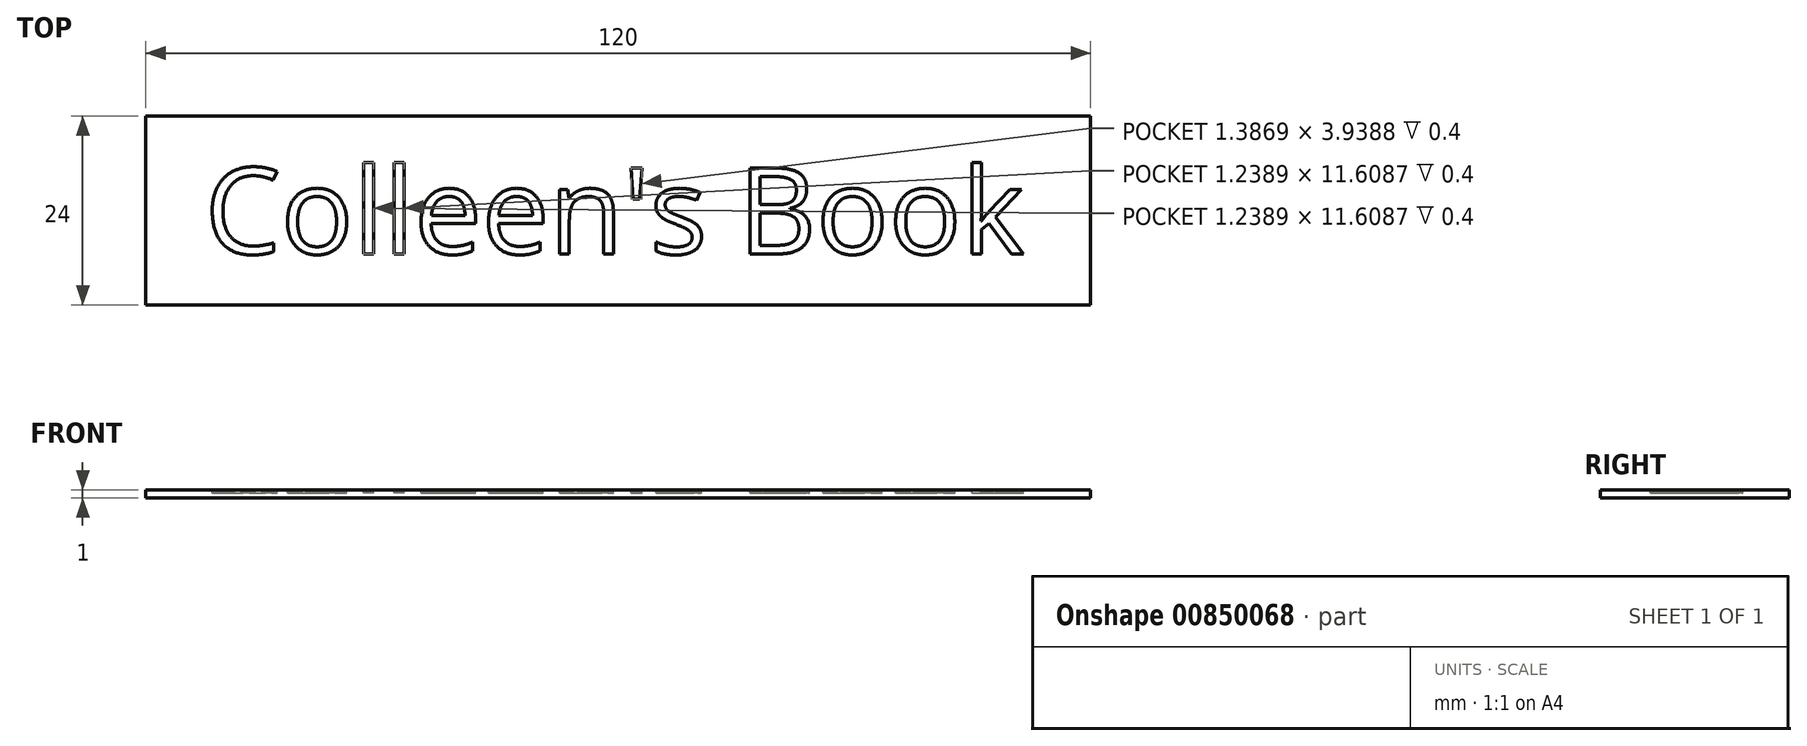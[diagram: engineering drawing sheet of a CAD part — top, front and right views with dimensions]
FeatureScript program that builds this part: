
annotation { "Feature Type Name" : "Feature", "Feature Type Description" : "" }
export const myFeature = defineFeature(function(context is Context, id is Id, definition is map)
    precondition{}
    {
        {
            var Q0;
            Q0=qCreatedBy(makeId("Top.planeOp"),FACE);
            var sketch = newSketch(context, id + "F0", { "sketchPlane" : qUnion([Q0])});
            skLineSegment(sketch, "E0.bottom", {"start": v(60, 12) * mm, "end": v(-60, 12) * mm});
            skLineSegment(sketch, "E0.top", {"start": v(60, -12) * mm, "end": v(-60, -12) * mm});
            skLineSegment(sketch, "E0.left", {"start": v(60, 12) * mm, "end": v(60, -12) * mm});
            skLineSegment(sketch, "E0.right", {"start": v(-60, 12) * mm, "end": v(-60, -12) * mm});
            skPoint(sketch, "E0.middle", {"position": v(0, 0) * mm});
            skSolve(sketch);
        }
        {
            var Q0;
            Q0 = qSketchRegion(id + "F0", true);
            extrude(context, id + "F1", {"entities" : qUnion([Q0]), "depth" : 1 * mm, "offsetDistance" : 25 * mm});
        }
        {
            var Q0;
            Q0=makeQuery(id+"F1.opExtrude","CAP_FACE",FACE,{"disambiguationData":[OSD([sQuery(id+"F0.wireOp",EDGE,"E0.bottom"),sQuery(id+"F0.wireOp",EDGE,"E0.top"),sQuery(id+"F0.wireOp",EDGE,"E0.left"),sQuery(id+"F0.wireOp",EDGE,"E0.right")])],"isStart":false});
            var sketch = newSketch(context, id + "F2", { "sketchPlane" : qUnion([Q0])});
            skLineSegment(sketch, "E1.0", {"start": v(-52.5, -5.5) * mm, "end": v(52.46, -5.5) * mm, "construction": true});
            skLineSegment(sketch, "E1.1", {"start": v(-52.5, 5.5) * mm, "end": v(-52.5, -5.5) * mm, "construction": true});
            skLineSegment(sketch, "E1.2", {"start": v(52.46, 5.5) * mm, "end": v(-52.5, 5.5) * mm, "construction": true});
            skLineSegment(sketch, "E1.3", {"start": v(52.46, -5.5) * mm, "end": v(52.46, 5.5) * mm, "construction": true});
            skText(sketch, "E2", { "text": "Colleen\'s Book", "fontName": "OpenSans-Regular.ttf"});
            const initialGuessF2  = {"E2": [-0.0525, -0.0055, 1, 0, 0.011]};
            skSetInitialGuess(sketch, initialGuessF2);
            skSolve(sketch);
        }
        {
            var Q0;
            Q0 = qSketchRegion(id + "F2", true);
            extrude(context, id + "F3", {"entities" : qUnion([Q0]), "operationType" : NewBodyOperationType.REMOVE, "oppositeDirection" : true, "depth" : .4 * mm, "offsetDistance" : 25 * mm});
        }
    });
